# Revit family: System_Furniture-Teknion-Typical-Height_Adjustable_Bench_Sit_Stand_03
name_source: partatom
category: Furniture Systems
revit_build: Autodesk Revit Architecture 2013 (Build: 20130531_2115(x64)
units: mm (PartAtom-declared; Revit-internal decimal feet)

## types (1)
- Height Adjustable-Bench Sit-Stand 03
    Additional Finishes = http://www.teknion.com
    Assembly Code = E2020200
    Description = 6’-0” x 5’-0” workstations or 18’-0” x 5’-0” overall cluster
    Environmental Data = http://www.teknion.com
    Height = 0' - 0"
    Item Code = Height Adjustable-Bench Sit-Stand 03
    Length = 5' - 0"
    Manufacturer = Teknion
    Manufacturer Fax = 416.661.4586
    Model = Height Adjustable-Bench Sit-Stand 03
    Product Line = Livello Height Adjustable Bench
    Product Page URL = http://teknionplanningtool.com
    URL = http://www.teknion.com
    Warranty = http://www.teknion.com
    Width = 18' - 0"

## geometry (parser evidence)
native form markers: Blend x32, Sweep x42
no freeform markers — native parametric forms only
